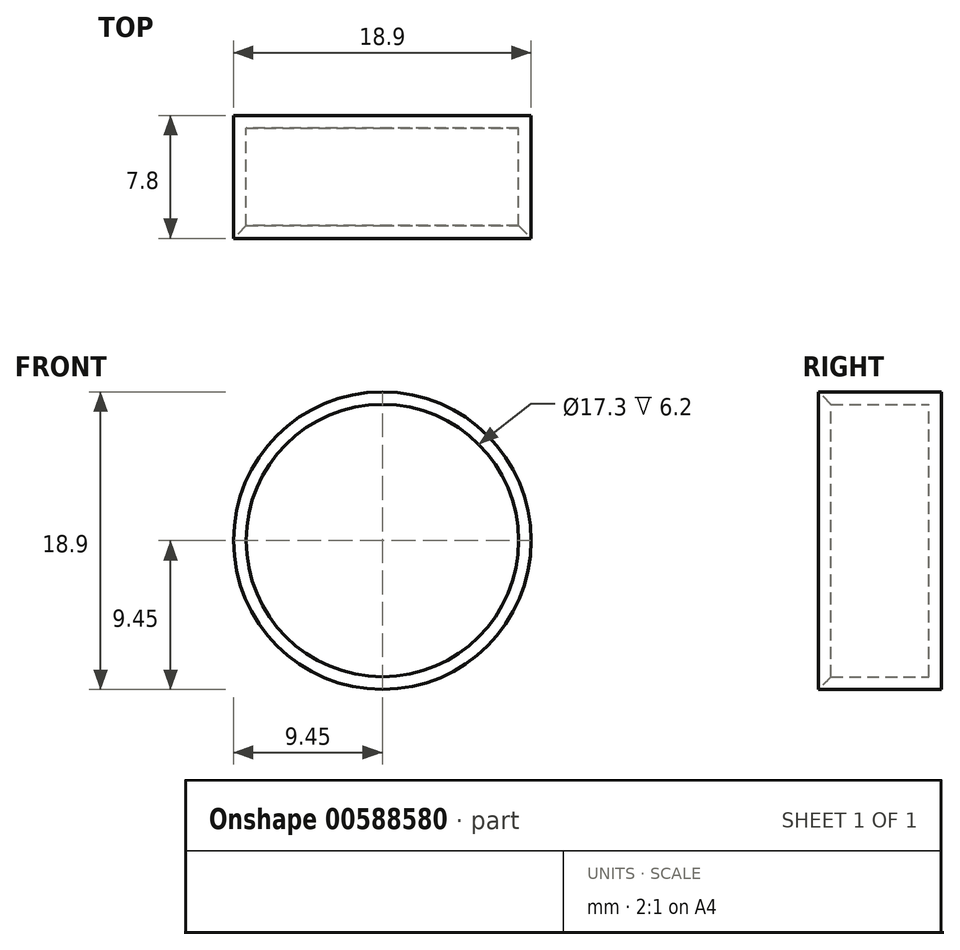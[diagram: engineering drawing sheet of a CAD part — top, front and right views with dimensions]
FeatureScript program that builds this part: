
annotation { "Feature Type Name" : "Feature", "Feature Type Description" : "" }
export const myFeature = defineFeature(function(context is Context, id is Id, definition is map)
    precondition{}
    {
        {
            var Q0;
            Q0=qCreatedBy(makeId("Front.planeOp"),FACE);
            var sketch = newSketch(context, id + "F0", { "sketchPlane" : qUnion([Q0])});
            skCircle(sketch, "E0", {"center": v(0, 0) * mm, "radius": 8.65 * mm});
            skCircle(sketch, "E1", {"center": v(0, 0) * mm, "radius": 9.45 * mm});
            skSolve(sketch);
        }
        {
            var Q0;
            Q0 = qSketchRegion(id + "F0", true);
            extrude(context, id + "F1", {"entities" : qUnion([Q0]), "depth" : 8 * mm, "offsetDistance" : 25 * mm});
        }
        {
            var Q0;
            Q0=qCreatedBy(makeId("Front.planeOp"),FACE);
            var sketch = newSketch(context, id + "F2", { "sketchPlane" : qUnion([Q0])});
            skCircle(sketch, "E2.0", {"center": v(0, 0) * mm, "radius": 8.65 * mm});
            skSolve(sketch);
        }
        {
            var Q0;
            Q0=makeQuery(id+"F2.imprint","IMPRINT",FACE,{"disambiguationData":[TD([[makeQuery(id+"F2.imprint","IMPRINT",EDGE,{"derivedFrom":sQuery(id+"F2.wireOp",EDGE,"E2.0")}),1.0]])]});
            extrude(context, id + "F3", {"entities" : qUnion([Q0]), "operationType" : NewBodyOperationType.ADD, "depth" : .8 * mm, "offsetDistance" : 25 * mm});
        }
        {
            var Q0;
            Q0=makeQuery(id+"F1.opExtrude","CAP_EDGE",EDGE,{"disambiguationData":[OSD([sQuery(id+"F0.wireOp",EDGE,"E0")])],"isStart":false});
            chamfer(context, id + "F4", {"entities" : qUnion([Q0]), "width" : 1 * mm, "tangentPropagation" : true});
        }
    });
